# Revit family: Sanitary_Showers_hansgrohe_24190XXX-Pulsify-Blend-Shower-set-105-3j_
name_source: partatom
category: Plumbing Fixtures
revit_build: Autodesk Revit 2018 (Build: 20170223_1515(x64)
units: mm (PartAtom-declared; Revit-internal decimal feet)

## family parameters
Always vertical = No
Cut with Voids When Loaded = No
OmniClass Number = 23.45.00.00
OmniClass Title = Sanitary, Laundry, and Cleaning Equipment
Part Type = Normal
Room Calculation Point = No
Round Connector Dimension = Use Diameter
Shared = No
Work Plane-Based = Yes

## types (1)
- 000 Chrome
    Always visible = Yes
    Default Elevation = 1219.2 mm  [stored 4 ft]
    Edition number = 0
    GTIN code = https://4059625347980
    Material 1 = Hansgrohe - Pulsify - 000 Chrome
    Material 2 = Hansgrohe - Pulsify - Graphite
    Product Guid = e5cabf85-acd4-4856-9e74-31e55c38c53f

note: [stored X ft] marks values corroborated as IEEE doubles in the binary element streams (Revit-internal decimal feet)

## geometry (parser evidence)
native form markers: Blend x1, Sweep x2
no freeform markers — native parametric forms only
